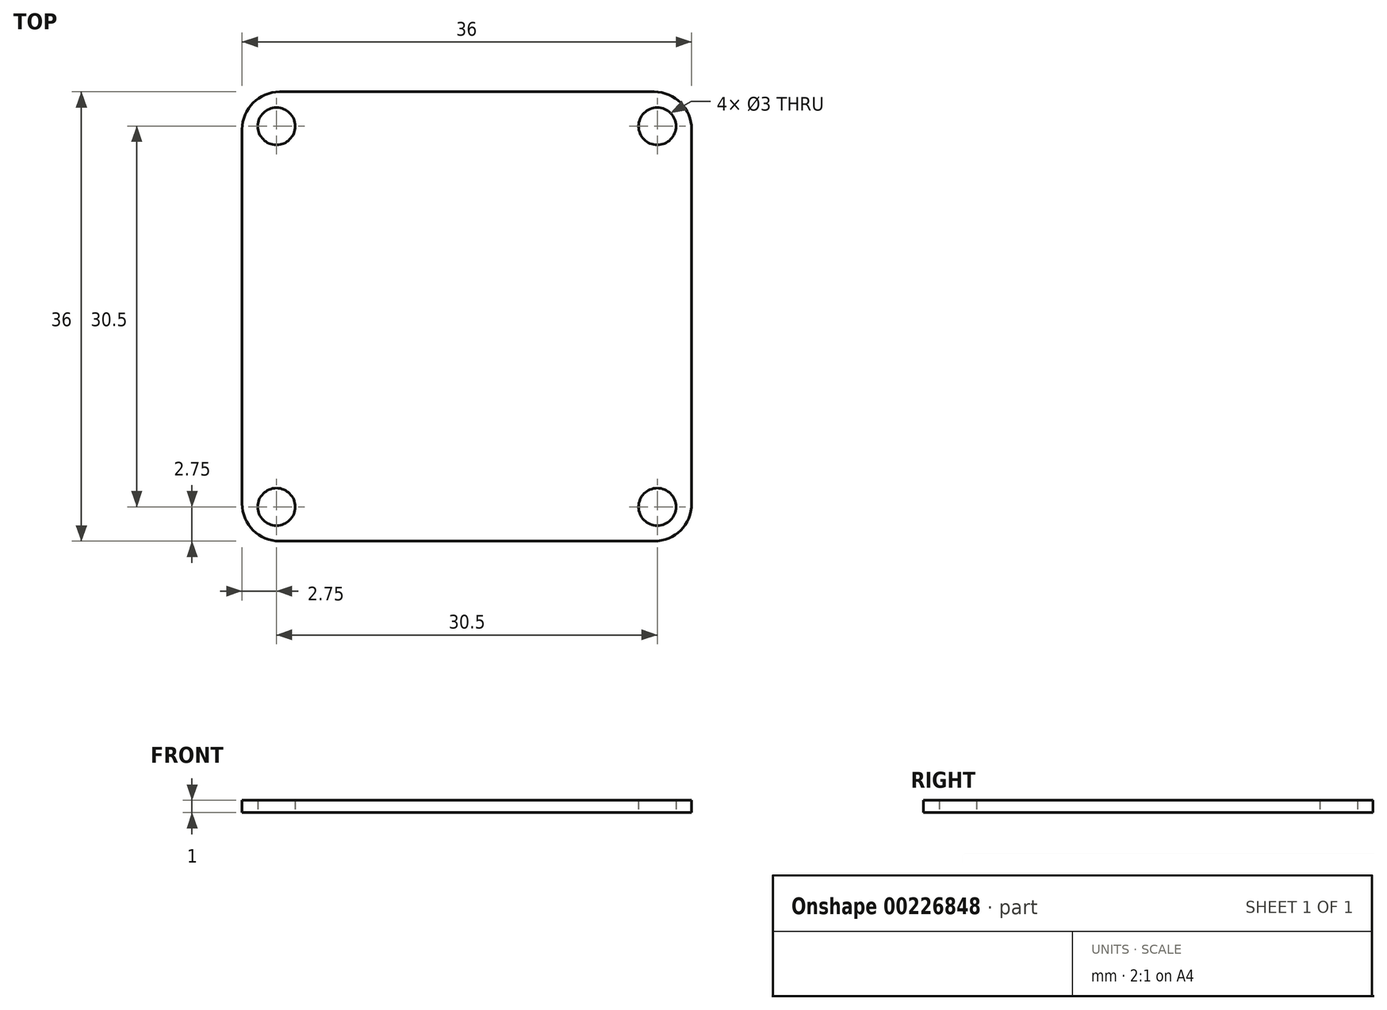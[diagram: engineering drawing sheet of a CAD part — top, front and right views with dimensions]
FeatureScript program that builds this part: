
annotation { "Feature Type Name" : "Feature", "Feature Type Description" : "" }
export const myFeature = defineFeature(function(context is Context, id is Id, definition is map)
    precondition{}
    {
        {
            var Q0;
            Q0=qCreatedBy(makeId("Top.planeOp"),FACE);
            var sketch = newSketch(context, id + "F0", { "sketchPlane" : qUnion([Q0])});
            skLineSegment(sketch, "E0.bottom", {"start": v(15, -18) * mm, "end": v(-15, -18) * mm});
            skLineSegment(sketch, "E0.top", {"start": v(15, 18) * mm, "end": v(-15, 18) * mm});
            skLineSegment(sketch, "E0.left", {"start": v(18, -15) * mm, "end": v(18, 15) * mm});
            skLineSegment(sketch, "E0.right", {"start": v(-18, -15) * mm, "end": v(-18, 15) * mm});
            skPoint(sketch, "E0.middle", {"position": v(0, 0) * mm});
            skLineSegment(sketch, "E1.bottom", {"start": v(15.25, -15.25) * mm, "end": v(-15.25, -15.25) * mm, "construction": true});
            skLineSegment(sketch, "E1.top", {"start": v(15.25, 15.25) * mm, "end": v(-15.25, 15.25) * mm, "construction": true});
            skLineSegment(sketch, "E1.left", {"start": v(15.25, -15.25) * mm, "end": v(15.25, 15.25) * mm, "construction": true});
            skLineSegment(sketch, "E1.right", {"start": v(-15.25, -15.25) * mm, "end": v(-15.25, 15.25) * mm, "construction": true});
            skCircle(sketch, "E2", {"center": v(-15.25, 15.25) * mm, "radius": 1.5 * mm});
            skCircle(sketch, "E3", {"center": v(15.25, 15.25) * mm, "radius": 1.5 * mm});
            skCircle(sketch, "E4", {"center": v(15.25, -15.25) * mm, "radius": 1.5 * mm});
            skCircle(sketch, "E5", {"center": v(-15.25, -15.25) * mm, "radius": 1.5 * mm});
            skPoint(sketch, "E6.visualSharp", {"position": v(-18, 18) * mm});
            skArc(sketch, "E6.filletArc", {"start": v(-15, 18) * mm, "mid": v(-17.12, 17.12) * mm, "end": v(-18, 15) * mm});
            skPoint(sketch, "E7.visualSharp", {"position": v(-18, -18) * mm});
            skArc(sketch, "E7.filletArc", {"start": v(-18, -15) * mm, "mid": v(-17.12, -17.12) * mm, "end": v(-15, -18) * mm});
            skPoint(sketch, "E8.visualSharp", {"position": v(18, -18) * mm});
            skArc(sketch, "E8.filletArc", {"start": v(15, -18) * mm, "mid": v(17.12, -17.12) * mm, "end": v(18, -15) * mm});
            skPoint(sketch, "E9.visualSharp", {"position": v(18, 18) * mm});
            skArc(sketch, "E9.filletArc", {"start": v(18, 15) * mm, "mid": v(17.12, 17.12) * mm, "end": v(15, 18) * mm});
            skSolve(sketch);
        }
        {
            var Q0;
            Q0 = qSketchRegion(id + "F0", true);
            extrude(context, id + "F1", {"entities" : qUnion([Q0]), "depth" : 1 * mm});
        }
    });
